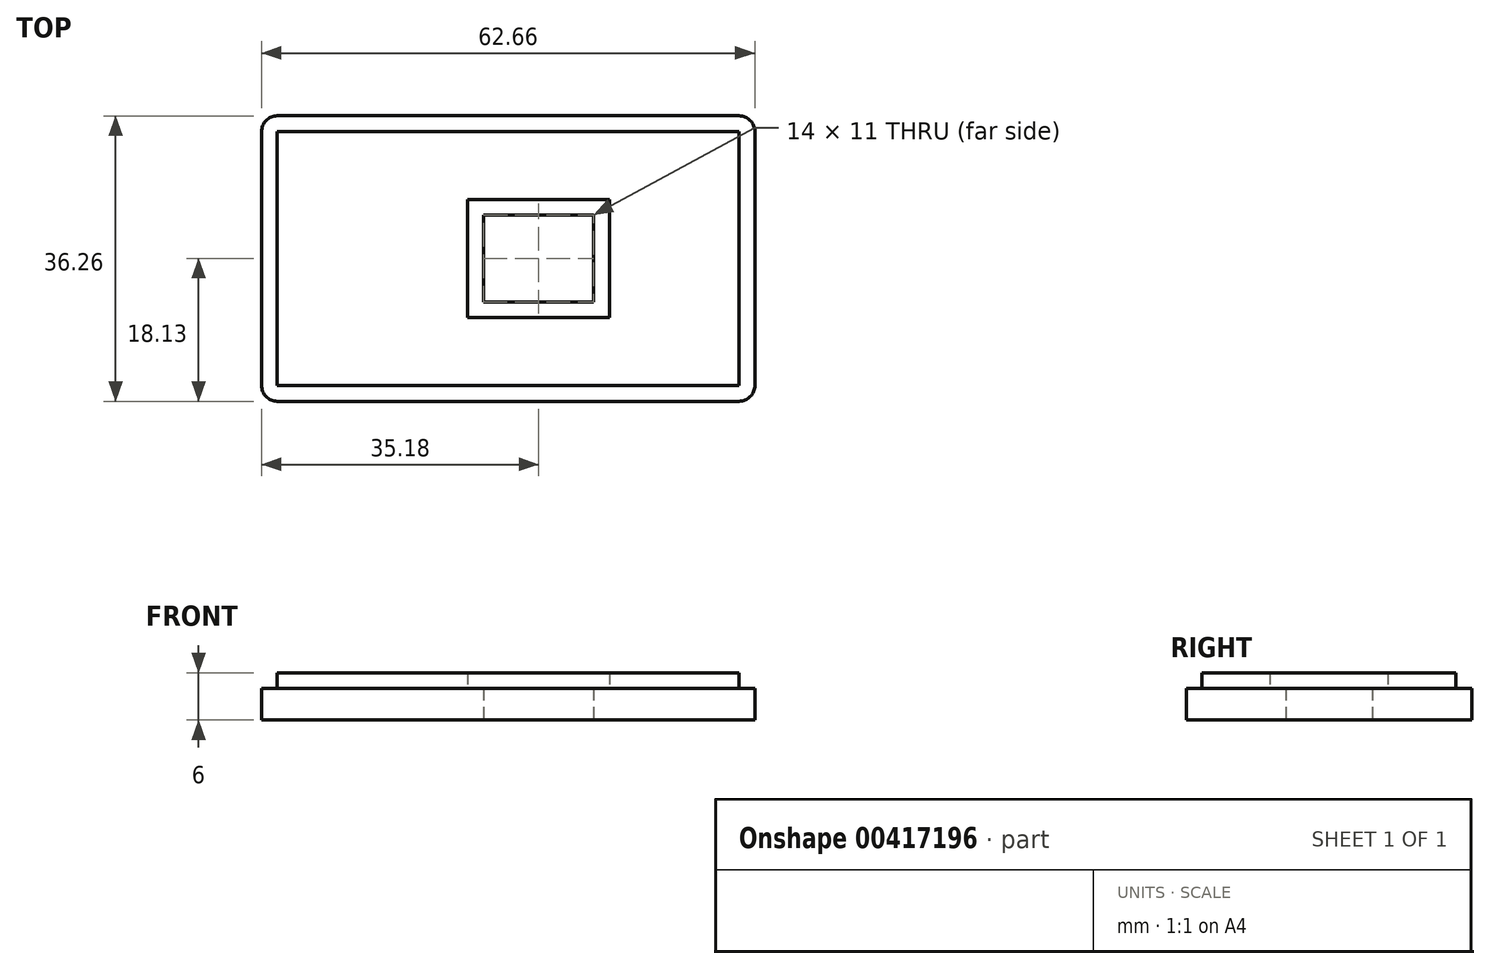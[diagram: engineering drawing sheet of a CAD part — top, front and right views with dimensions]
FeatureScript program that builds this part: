
annotation { "Feature Type Name" : "Feature", "Feature Type Description" : "" }
export const myFeature = defineFeature(function(context is Context, id is Id, definition is map)
    precondition{}
    {
        {
            var Q0;
            Q0=qCreatedBy(makeId("Top.planeOp"),FACE);
            var sketch = newSketch(context, id + "F0", { "sketchPlane" : qUnion([Q0])});
            skLineSegment(sketch, "E0.bottom", {"start": v(-33.18, -16.13) * mm, "end": v(25.48, -16.13) * mm});
            skLineSegment(sketch, "E0.top", {"start": v(-33.18, 16.13) * mm, "end": v(25.48, 16.13) * mm});
            skLineSegment(sketch, "E0.left", {"start": v(-33.18, -16.13) * mm, "end": v(-33.18, 16.13) * mm});
            skLineSegment(sketch, "E0.right", {"start": v(25.48, -16.13) * mm, "end": v(25.48, 16.13) * mm});
            skLineSegment(sketch, "E1.bottom", {"start": v(9, 7.5) * mm, "end": v(-9, 7.5) * mm});
            skLineSegment(sketch, "E1.top", {"start": v(9, -7.5) * mm, "end": v(-9, -7.5) * mm});
            skLineSegment(sketch, "E1.left", {"start": v(9, 7.5) * mm, "end": v(9, -7.5) * mm});
            skLineSegment(sketch, "E1.right", {"start": v(-9, 7.5) * mm, "end": v(-9, -7.5) * mm});
            skPoint(sketch, "E1.middle", {"position": v(0, 0) * mm});
            skSolve(sketch);
        }
        {
            var Q0;
            Q0=makeQuery(id+"F0.imprint","IMPRINT",FACE,{"disambiguationData":[TD([[makeQuery(id+"F0.imprint","IMPRINT",EDGE,{"derivedFrom":sQuery(id+"F0.wireOp",EDGE,"KOcZIAKO-d5oq-UWk9-kR2x-IdMk12HUyKKo")}),1.0]])]});
            var Q1;
            Q1=makeQuery(id+"F0.imprint","IMPRINT",FACE,{"disambiguationData":[TD([[makeQuery(id+"F0.imprint","IMPRINT",EDGE,{"derivedFrom":sQuery(id+"F0.wireOp",EDGE,"KhAvUVLq-ho8g-pRxV-bAmC-bZWq5vJV3irS")}),1.0]])]});
            var Q2;
            Q2=makeQuery(id+"F0.imprint","IMPRINT",FACE,{"disambiguationData":[TD([[makeQuery(id+"F0.imprint","IMPRINT",EDGE,{"derivedFrom":sQuery(id+"F0.wireOp",EDGE,"acC1lYdK-YMS1-WjWr-tsKV-B5pZz2fk9CDq")}),1.0]])]});
            var Q3;
            Q3=makeQuery(id+"F0.imprint","IMPRINT",FACE,{"disambiguationData":[TD([[makeQuery(id+"F0.imprint","IMPRINT",EDGE,{"derivedFrom":sQuery(id+"F0.wireOp",EDGE,"V2kgQMwl-wZXp-MItN-56oV-F2BPTq4mBUci")}),1.0]])]});
            var Q4;
            Q4=makeQuery(id+"F0.imprint","IMPRINT",FACE,{"disambiguationData":[TD([[makeQuery(id+"F0.imprint","IMPRINT",EDGE,{"derivedFrom":sQuery(id+"F0.wireOp",EDGE,"E0.bottom")}),1.0]])]});
            extrude(context, id + "F1", {"entities" : qUnion([Q0, Q1, Q2, Q3, Q4]), "depth" : 2 * mm});
        }
        {
            var Q0;
            Q0=makeQuery(id+"F1.opExtrude","CAP_FACE",FACE,{"disambiguationData":[OSD([sQuery(id+"F0.wireOp",EDGE,"E0.bottom"),sQuery(id+"F0.wireOp",EDGE,"E0.top"),sQuery(id+"F0.wireOp",EDGE,"E0.left"),sQuery(id+"F0.wireOp",EDGE,"E0.right")])],"isStart":false});
            shell(context, id + "F2", {"entities" : qUnion([Q0]), "thickness" : 2 * mm, "oppositeDirection" : true});
        }
        {
            var Q0;
            Q0=makeQuery(id+"F1.opExtrude","SWEPT_EDGE",EDGE,{"disambiguationData":[OSD([sQuery(id+"F0.wireOp",EDGE,"E0.top"),sQuery(id+"F0.wireOp",EDGE,"E0.left")])]});
            var Q1;
            Q1=makeQuery(id+"F1.opExtrude","SWEPT_EDGE",EDGE,{"disambiguationData":[OSD([sQuery(id+"F0.wireOp",EDGE,"E0.bottom"),sQuery(id+"F0.wireOp",EDGE,"E0.left")])]});
            var Q2;
            Q2=makeQuery(id+"F1.opExtrude","SWEPT_EDGE",EDGE,{"disambiguationData":[OSD([sQuery(id+"F0.wireOp",EDGE,"E0.bottom"),sQuery(id+"F0.wireOp",EDGE,"E0.right")])]});
            var Q3;
            Q3=makeQuery(id+"F1.opExtrude","SWEPT_EDGE",EDGE,{"disambiguationData":[OSD([sQuery(id+"F0.wireOp",EDGE,"E0.top"),sQuery(id+"F0.wireOp",EDGE,"E0.right")])]});
            fillet(context, id + "F3", {"entities" : qUnion([Q0, Q1, Q2, Q3]), "radius" : 2 * mm, "tangentPropagation" : true, "allowEdgeOverflow" : false});
        }
        {
            var Q0;
            Q0=makeQuery(id+"F0.imprint","IMPRINT",FACE,{"disambiguationData":[TD([[makeQuery(id+"F0.imprint","IMPRINT",EDGE,{"derivedFrom":sQuery(id+"F0.wireOp",EDGE,"E0.bottom")}),1.0]])]});
            extrude(context, id + "F4", {"entities" : qUnion([Q0]), "operationType" : NewBodyOperationType.ADD, "depth" : 4 * mm});
        }
    });
